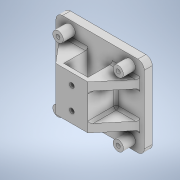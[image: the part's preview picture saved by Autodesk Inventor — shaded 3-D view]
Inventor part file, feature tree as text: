
AUTODESK INVENTOR PART (.ipt)
format: ipt  version: 2022.2 (Build 262287010, 287A)  size: 552,960 bytes
history: native  units: mm
features: extrude x12, sketch x10, other x7, fillet x3, mirror x1
ambient origin geometry x8: Origin, YZ Plane, XZ Plane, XY Plane, X Axis, Y Axis, Z Axis, Center Point
bodies: Body1 (feature_tree)
feature tree (33):
  other  "Твердое тело1"
  extrude  "Выдавливание1"  Depth=135.0mm
  sketch  "Эскиз2"
  extrude  "Выдавливание2"  Depth=110.0mm
  extrude  "Выдавливание3"  Depth=10.0mm TaperAngle=0.0deg
  extrude  "Выдавливание4"  Depth=24.0mm
  other  "РабПлоскость5"
  extrude  "Выдавливание7"  Depth=5.1mm
  extrude  "Выдавливание8"  Depth=20.0mm
  extrude  "Выдавливание9"  TaperAngle=0.0deg  [1 undecoded]
  sketch  "Эскиз14"
  extrude  "Выдавливание10"  Depth=30.2mm TaperAngle=0.0deg
  extrude  "Выдавливание11"  Depth=5.0mm TaperAngle=0.0deg
  extrude  "Выдавливание12"  [1 undecoded]
  extrude  "Выдавливание13"  Depth=3.3mm
  other  "Удаление грани1"
  other  "РабПлоскость6"
  mirror  "Зеркальное отражение1"
  fillet  "Сопряжение1"  Radius=31.0mm
  fillet  "Сопряжение2"  Radius=5.0mm
  fillet  "Сопряжение3"  Radius=30.2mm
  other  "Непосредственное редактирование1"
  extrude  "Выдавливание14"  Depth=10.0mm TaperAngle=0.0deg
  sketch  "Эскиз1"
  sketch  "Эскиз3"
  sketch  "Эскиз11"
  sketch  "Эскиз12"
  sketch  "Эскиз13"
  sketch  "Эскиз15"
  sketch  "Эскиз16"
  sketch  "Эскиз17"
  other  "Перенос1"
  other  "Перенос2"
note: 2 required parameter values undecoded (feature->parameter linkage not recoverable at this tier; creation-order binding heuristic only, values carry confidence <= 0.55)
